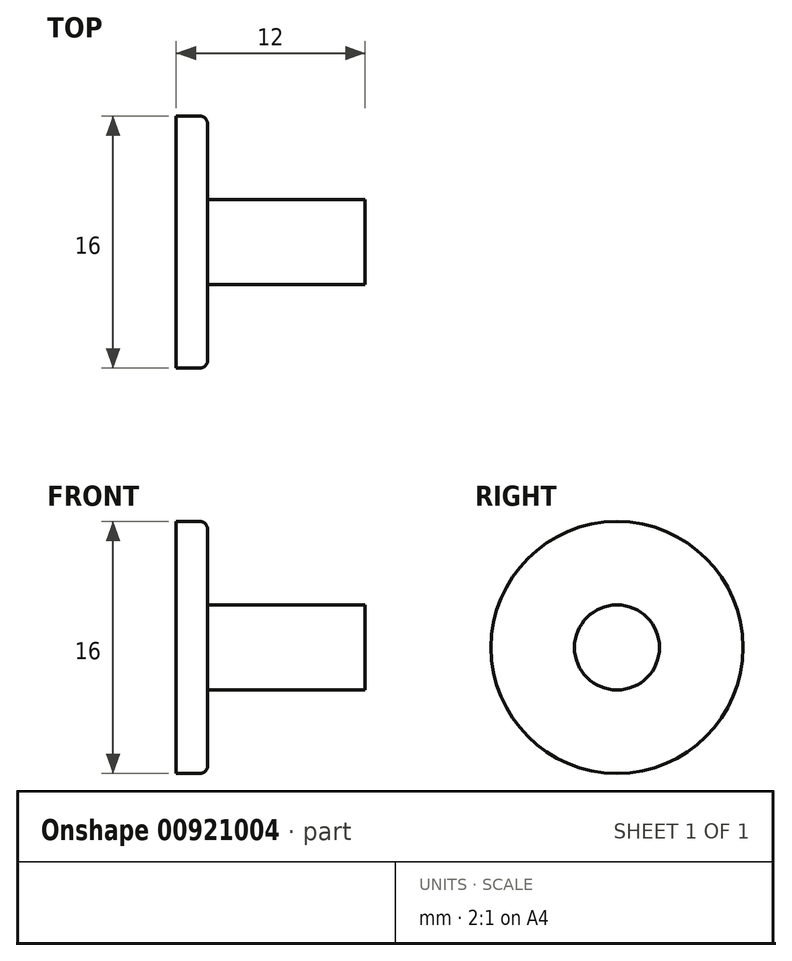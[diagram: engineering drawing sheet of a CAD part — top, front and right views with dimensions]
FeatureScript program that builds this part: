
annotation { "Feature Type Name" : "Feature", "Feature Type Description" : "" }
export const myFeature = defineFeature(function(context is Context, id is Id, definition is map)
    precondition{}
    {
        {
            var Q0;
            Q0=qCreatedBy(makeId("Right.planeOp"),FACE);
            var sketch = newSketch(context, id + "F0", { "sketchPlane" : qUnion([Q0])});
            skCircle(sketch, "E0", {"center": v(-26.54, 17.84) * mm, "radius": 8 * mm});
            skSolve(sketch);
        }
        {
            var Q0;
            Q0=qSketchRegion(id+"F0",true);
            extrude(context, id + "F1", {"entities" : qUnion([Q0]), "depth" : 2 * mm, "offsetDistance" : 25 * mm});
        }
        {
            var Q0;
            Q0=makeQuery(id+"F1.opExtrude","CAP_FACE",FACE,{"disambiguationData":[OSD([sQuery(id+"F0.wireOp",EDGE,"E0")])],"isStart":false});
            var sketch = newSketch(context, id + "F2", { "sketchPlane" : qUnion([Q0])});
            skCircle(sketch, "E1", {"center": v(-26.54, 17.84) * mm, "radius": 2.7 * mm});
            skSolve(sketch);
        }
        {
            var Q0;
            Q0=makeQuery(id+"F2.imprint","IMPRINT",FACE,{"disambiguationData":[TD([[makeQuery(id+"F2.imprint","IMPRINT",EDGE,{"derivedFrom":sQuery(id+"F2.wireOp",EDGE,"E1")}),1.0]])]});
            extrude(context, id + "F3", {"entities" : qUnion([Q0]), "operationType" : NewBodyOperationType.ADD, "depth" : 10 * mm, "offsetDistance" : 25 * mm});
        }
        {
            var Q0;
            Q0=makeQuery(id+"F1.opExtrude","CAP_EDGE",EDGE,{"disambiguationData":[OSD([sQuery(id+"F0.wireOp",EDGE,"E0")])],"isStart":false});
            fillet(context, id + "F4", {"entities" : qUnion([Q0]), "radius" : 0.5 * mm, "tangentPropagation" : true, "allowEdgeOverflow" : false});
        }
    });
